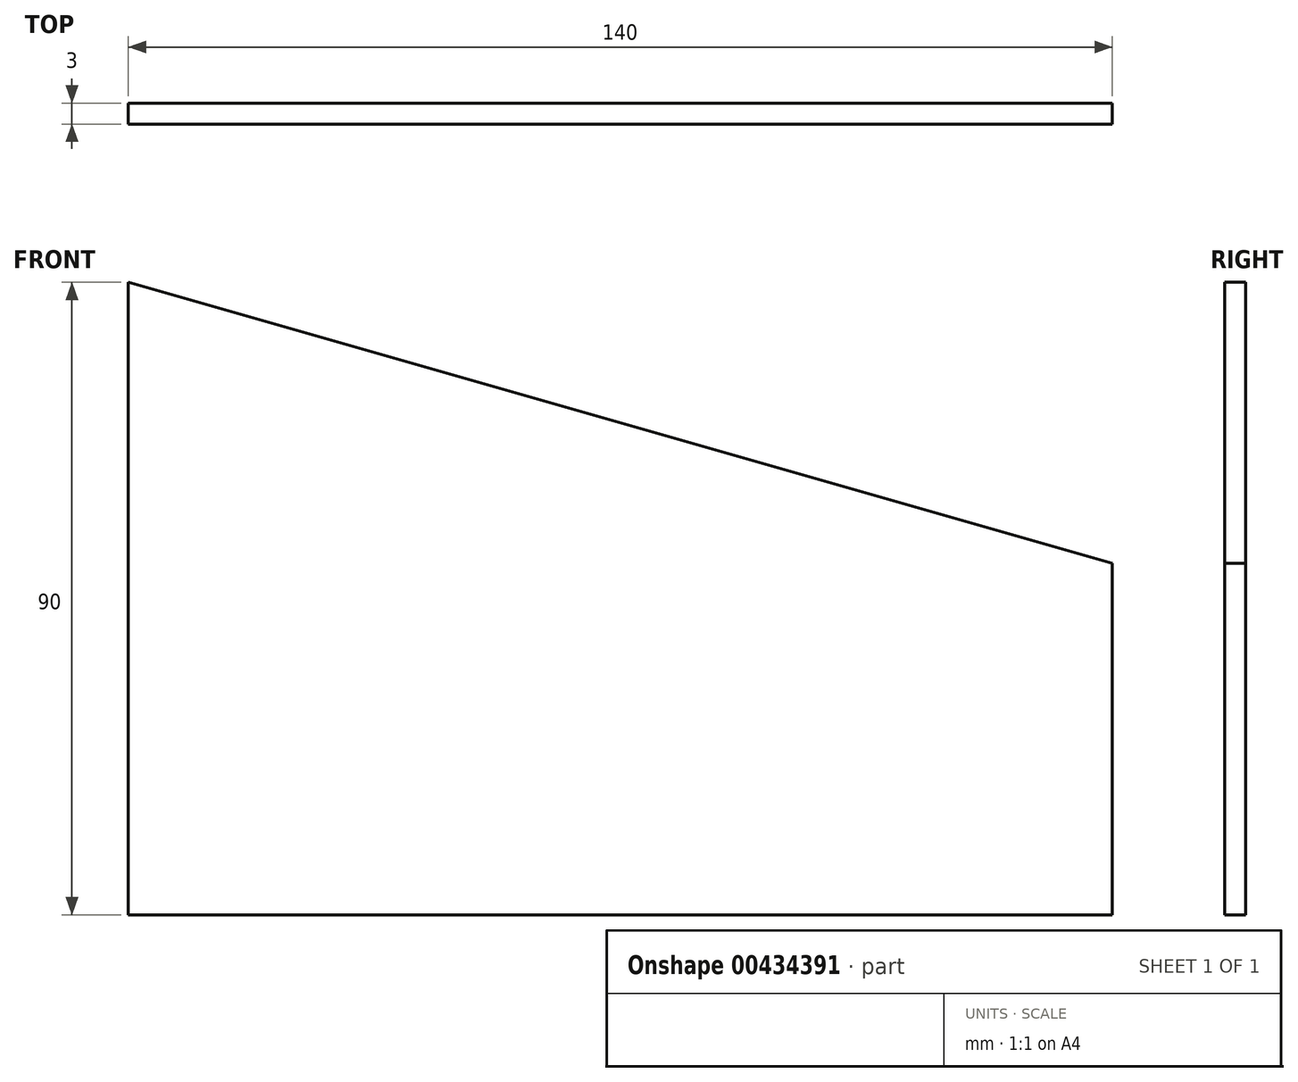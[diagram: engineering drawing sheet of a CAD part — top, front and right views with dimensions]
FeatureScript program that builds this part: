
annotation { "Feature Type Name" : "Feature", "Feature Type Description" : "" }
export const myFeature = defineFeature(function(context is Context, id is Id, definition is map)
    precondition{}
    {
        {
            var Q0;
            Q0=qCreatedBy(makeId("Front.planeOp"),FACE);
            var sketch = newSketch(context, id + "F0", { "sketchPlane" : qUnion([Q0])});
            skLineSegment(sketch, "E0.bottom", {"start": v(0, 0) * mm, "end": v(140, 0) * mm});
            skLineSegment(sketch, "E0.left", {"start": v(0, 0) * mm, "end": v(0, 90) * mm});
            skLineSegment(sketch, "E0.right", {"start": v(140, 0) * mm, "end": v(140, 50) * mm});
            skLineSegment(sketch, "E1", {"start": v(0, 90) * mm, "end": v(140, 50) * mm});
            skSolve(sketch);
        }
        {
            var Q0;
            Q0 = qSketchRegion(id + "F0", true);
            extrude(context, id + "F1", {"entities" : qUnion([Q0]), "depth" : 3 * mm});
        }
    });
